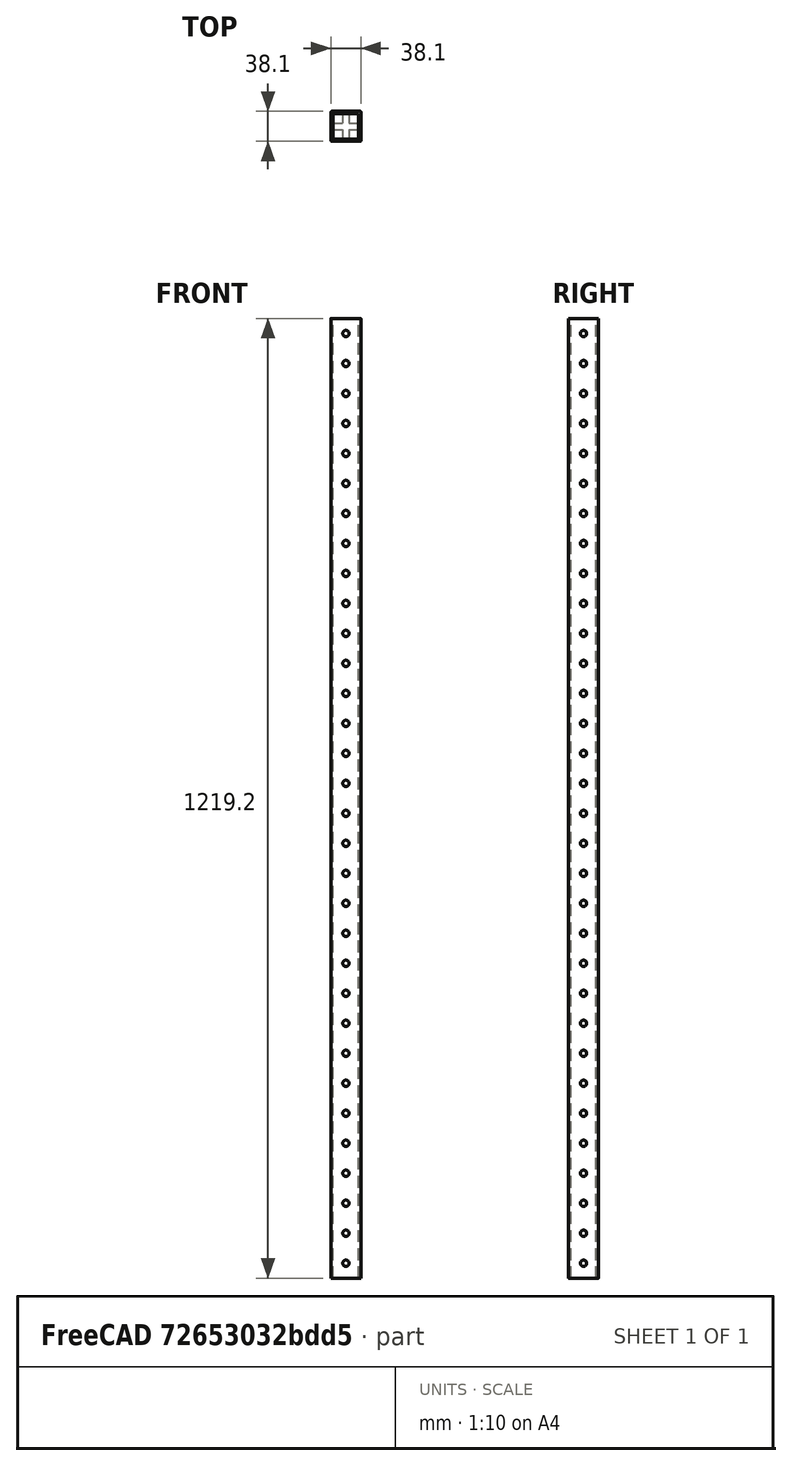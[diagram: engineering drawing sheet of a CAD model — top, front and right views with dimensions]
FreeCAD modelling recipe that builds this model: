
FCSTD DOCUMENT  (FreeCAD 0.15R4671 (Git))
Label: base-model-fillet
License: All rights reserved
LicenseURL: http://en.wikipedia.org/wiki/All_rights_reserved
objects: Part::Box×2, Part::Cylinder×2, Part::FeaturePython×2, PartDesign::Fillet×1
note: 7 computed .brp shape members not serialized (recipe doc carries the construction recipe); baked Part::Feature solids carry a one-line shape summary decoded from their .brp

FEATURE [Part::Box] Box  label="Beam"
  Height = 1219.2
  Length = 38.1
  Width = 38.1
FEATURE [Part::Cylinder] Cylinder
  Angle = 360
  Height = 38.1
  Placement = pos=(0,19.05,19.05) rot=(0,1,0;1.5708rad)
  Radius = 4
FEATURE [Part::Cylinder] Cylinder001
  Angle = 360
  Height = 38.1
  Placement = pos=(19.05,38.1,19.05) rot=(1,0,0;1.5708rad)
  Radius = 4
FEATURE [Part::FeaturePython] Array  label="Holes1"  # Draft array (typed FeaturePython)
  Angle = 360
  ArrayType = 0
  Axis = (0,0,1)
  Base = -> Cylinder001
  Center = (0,0,0)
  Fuse = false
  IntervalAxis = (0,0,0)
  IntervalX = (1,0,0)
  IntervalY = (0,1,0)
  IntervalZ = (0,0,38.1)
  NumberPolar = 1
  NumberX = 1
  NumberY = 1
  NumberZ = 32
FEATURE [Part::FeaturePython] Array001  label="Holes2"  # Draft array (typed FeaturePython)
  Angle = 360
  ArrayType = 0
  Axis = (0,0,1)
  Base = -> Cylinder
  Center = (0,0,0)
  Fuse = false
  IntervalAxis = (0,0,0)
  IntervalX = (1,0,0)
  IntervalY = (0,1,0)
  IntervalZ = (0,0,38.1)
  NumberPolar = 1
  NumberX = 1
  NumberY = 1
  NumberZ = 32
FEATURE [Part::Box] Box001  label="Cutout"
  Height = 1219.2
  Length = 32.1
  Placement = pos=(3,3,0) rot=(0,0,1;0rad)
  Width = 32.1
FEATURE [PartDesign::Fillet] Fillet
  Base = -> Box [Edge1,Edge5,Edge7,Edge3]
  Radius = 1
